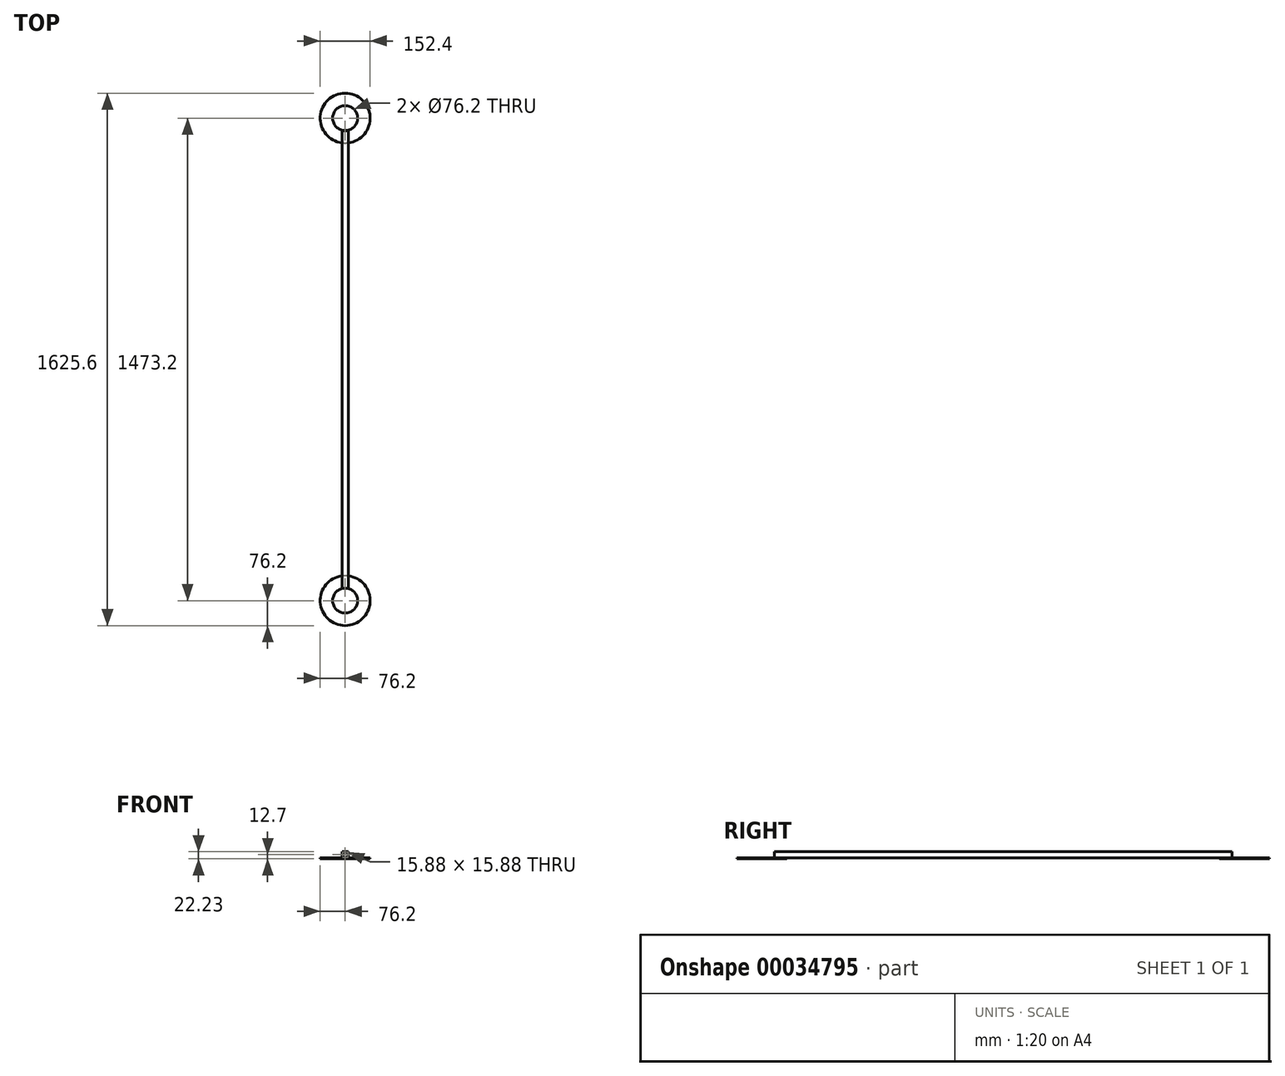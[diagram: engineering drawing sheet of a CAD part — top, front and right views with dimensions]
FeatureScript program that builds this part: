
annotation { "Feature Type Name" : "Feature", "Feature Type Description" : "" }
export const myFeature = defineFeature(function(context is Context, id is Id, definition is map)
    precondition{}
    {
        {
            var Q0;
            Q0=qCreatedBy(makeId("Front.planeOp"),FACE);
            var sketch = newSketch(context, id + "F0", { "sketchPlane" : qUnion([Q0])});
            skLineSegment(sketch, "E0.rect.bottom", {"start": v(9.53, 9.53) * mm, "end": v(-9.53, 9.53) * mm});
            skLineSegment(sketch, "E0.rect.top", {"start": v(9.53, -9.52) * mm, "end": v(-9.53, -9.52) * mm});
            skLineSegment(sketch, "E0.rect.left", {"start": v(9.53, 9.53) * mm, "end": v(9.53, -9.52) * mm});
            skLineSegment(sketch, "E0.rect.right", {"start": v(-9.53, 9.53) * mm, "end": v(-9.53, -9.52) * mm});
            skPoint(sketch, "E0.rect.middle", {"position": v(0, 0) * mm});
            skLineSegment(sketch, "E1.0", {"start": v(7.94, 7.94) * mm, "end": v(-7.94, 7.94) * mm});
            skLineSegment(sketch, "E1.1", {"start": v(7.94, 7.94) * mm, "end": v(7.94, -7.94) * mm});
            skLineSegment(sketch, "E1.2", {"start": v(7.94, -7.94) * mm, "end": v(-7.94, -7.94) * mm});
            skLineSegment(sketch, "E1.3", {"start": v(-7.94, 7.94) * mm, "end": v(-7.94, -7.94) * mm});
            skSolve(sketch);
        }
        {
            var Q0;
            Q0=makeQuery(id+"F0.imprint","IMPRINT",FACE,{"disambiguationData":[TD([[makeQuery(id+"F0.imprint","IMPRINT",EDGE,{"derivedFrom":sQuery(id+"F0.wireOp",EDGE,"E0.rect.bottom")}),1.0]])]});
            extrude(context, id + "F1", {"entities" : qUnion([Q0]), "depth" : 1397 * mm});
        }
        {
            var Q0;
            Q0=makeQuery(id+"F1.opExtrude","SWEPT_FACE",FACE,{"disambiguationData":[OSD([sQuery(id+"F0.wireOp",EDGE,"E0.rect.top")])]});
            var sketch = newSketch(context, id + "F2", { "sketchPlane" : qUnion([Q0])});
            skCircle(sketch, "E2", {"center": v(0, -38.1) * mm, "radius": 76.2 * mm});
            skPoint(sketch, "E2.centerSnap0", {"position": v(0, 0) * mm});
            skCircle(sketch, "E3", {"center": v(0, -38.1) * mm, "radius": 38.1 * mm});
            skSolve(sketch);
        }
        {
            var Q0;
            {var subQ2=sQuery(id+"F2.wireOp",EDGE,"E3");Q0=makeQuery(id+"F2.imprint","IMPRINT",FACE,{"disambiguationData":[TD([[makeQuery(id+"F2.imprint","IMPRINT",EDGE,{"derivedFrom":subQ2}),-1.0]])]});}
            var Q1;
            {var subQ0=sQuery(id+"F0.wireOp",EDGE,"E0.rect.top");var subQ1=makeQuery(id+"F1.opExtrude","CAP_EDGE",EDGE,{"disambiguationData":[OSD([subQ0])],"isStart":true});var subQ2=makeQuery(id+"F2.imprint","INTERSECT",VERTEX,{"derivedFrom":[subQ1,sQuery(id+"F2.wireOp",EDGE,"E3")]});Q1=makeQuery(id+"F2.imprint","IMPRINT",FACE,{"disambiguationData":[TD([[makeQuery(id+"F2.imprint","IMPRINT",EDGE,{"disambiguationData":[TD([[subQ2,1.0]])],"derivedFrom":subQ1}),-1.0]])]});}
            extrude(context, id + "F3", {"entities" : qUnion([Q0, Q1]), "operationType" : NewBodyOperationType.ADD, "depth" : 3.17 * mm});
        }
        {
            var Q0;
            Q0=makeQuery(id+"F1.opExtrude","SWEPT_FACE",FACE,{"disambiguationData":[OSD([sQuery(id+"F0.wireOp",EDGE,"E0.rect.top")])]});
            var sketch = newSketch(context, id + "F4", { "sketchPlane" : qUnion([Q0])});
            skCircle(sketch, "E4", {"center": v(0, 1435.1) * mm, "radius": 76.2 * mm});
            skCircle(sketch, "E5", {"center": v(0, 1435.1) * mm, "radius": 38.1 * mm});
            skSolve(sketch);
        }
        {
            var Q0;
            {var subQ16=sQuery(id+"F4.wireOp",EDGE,"E5");Q0=makeQuery(id+"F4.imprint","IMPRINT",FACE,{"disambiguationData":[TD([[makeQuery(id+"F4.imprint","IMPRINT",EDGE,{"derivedFrom":subQ16}),-1.0]])]});}
            var Q1;
            {var subQ0=sQuery(id+"F0.wireOp",EDGE,"E0.rect.top");var subQ11=makeQuery(id+"F1.opExtrude","CAP_EDGE",EDGE,{"disambiguationData":[OSD([subQ0])],"isStart":false});var subQ15=makeQuery(id+"F4.imprint","INTERSECT",VERTEX,{"derivedFrom":[subQ11,sQuery(id+"F4.wireOp",EDGE,"E5")]});Q1=makeQuery(id+"F4.imprint","IMPRINT",FACE,{"disambiguationData":[TD([[makeQuery(id+"F4.imprint","IMPRINT",EDGE,{"disambiguationData":[TD([[subQ15,1.0]])],"derivedFrom":subQ11}),1.0]])]});}
            extrude(context, id + "F5", {"entities" : qUnion([Q0, Q1]), "operationType" : NewBodyOperationType.ADD, "depth" : 3.17 * mm});
        }
    });
